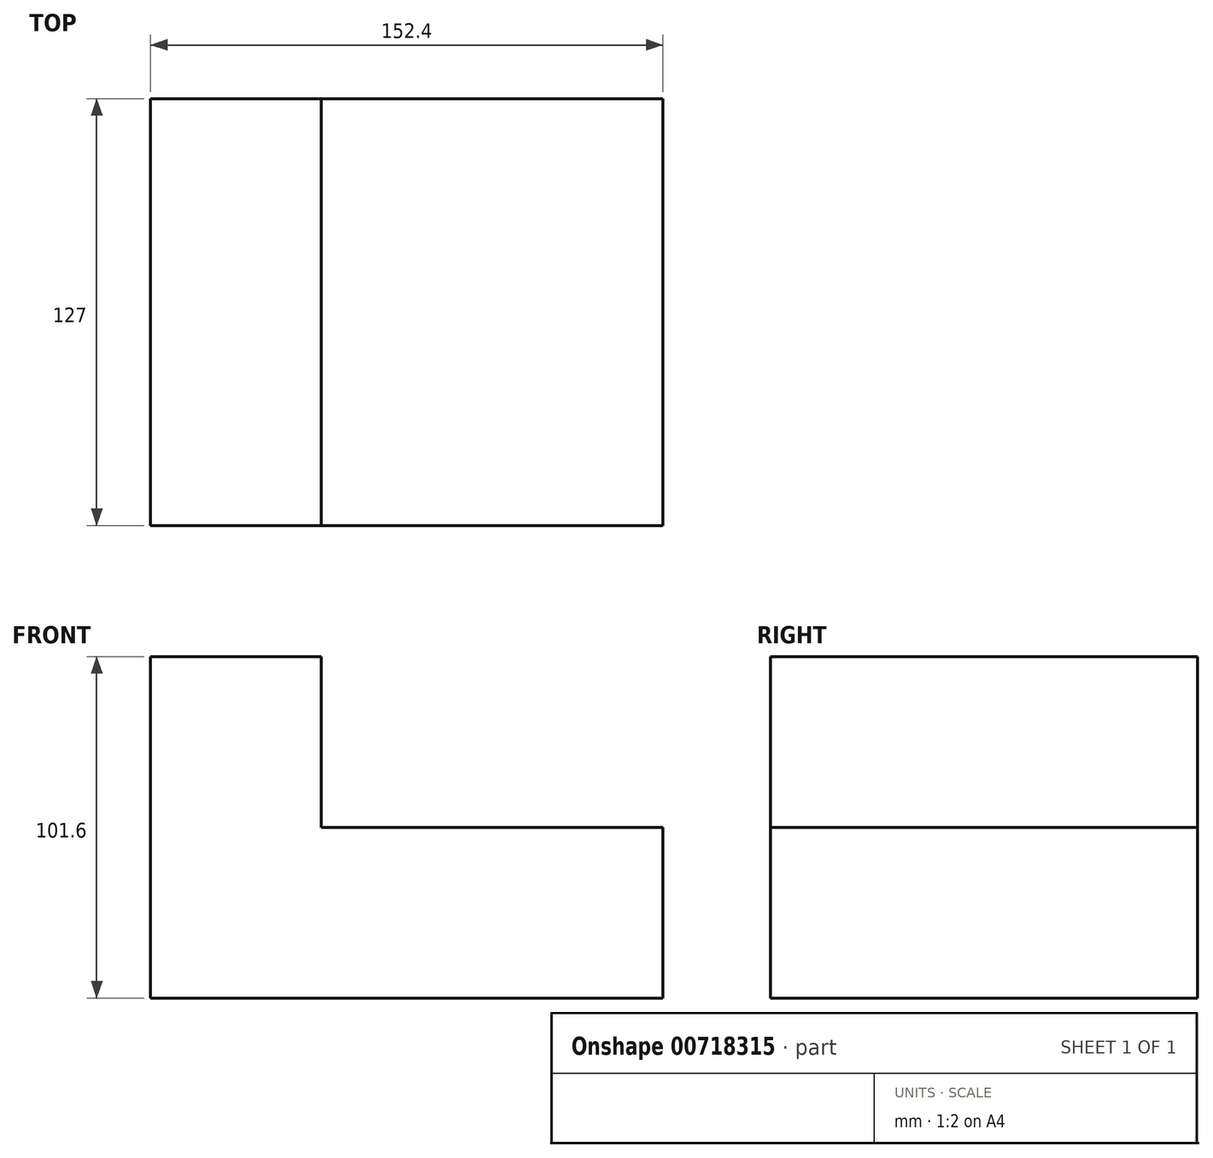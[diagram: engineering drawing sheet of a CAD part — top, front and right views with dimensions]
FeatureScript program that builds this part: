
annotation { "Feature Type Name" : "Feature", "Feature Type Description" : "" }
export const myFeature = defineFeature(function(context is Context, id is Id, definition is map)
    precondition{}
    {
        {
            var Q0;
            Q0=qCreatedBy(makeId("Front.planeOp"),FACE);
            var sketch = newSketch(context, id + "F0", { "sketchPlane" : qUnion([Q0])});
            skLineSegment(sketch, "E0", {"start": v(-56.64, -38.14) * mm, "end": v(-56.64, 63.46) * mm});
            skLineSegment(sketch, "E1", {"start": v(-56.64, -38.14) * mm, "end": v(95.76, -38.14) * mm});
            skLineSegment(sketch, "E2", {"start": v(95.76, -38.14) * mm, "end": v(95.76, 12.66) * mm});
            skLineSegment(sketch, "E3", {"start": v(-5.84, 18.67) * mm, "end": v(-5.84, 12.66) * mm});
            skLineSegment(sketch, "E4", {"start": v(-5.84, 12.66) * mm, "end": v(95.76, 12.66) * mm});
            skLineSegment(sketch, "E5", {"start": v(-5.84, 18.67) * mm, "end": v(-5.84, 63.46) * mm});
            skLineSegment(sketch, "E6", {"start": v(-56.64, 63.46) * mm, "end": v(-5.84, 63.46) * mm});
            skSolve(sketch);
        }
        {
            var Q0;
            Q0=makeQuery(id+"F0.imprint","IMPRINT",FACE,{"disambiguationData":[TD([[makeQuery(id+"F0.imprint","IMPRINT",EDGE,{"derivedFrom":sQuery(id+"F0.wireOp",EDGE,"E0")}),-1.0]])]});
            extrude(context, id + "F1", {"entities" : qUnion([Q0]), "depth" : 127 * mm, "offsetDistance" : 25.4 * mm});
        }
    });
